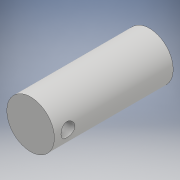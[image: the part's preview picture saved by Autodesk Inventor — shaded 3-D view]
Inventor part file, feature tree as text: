
AUTODESK INVENTOR PART (.ipt)
format: ipt  version: 2018 (Build 220112000, 112)  size: 106,496 bytes
history: native  units: mm
features: extrude x2, sketch x2
ambient origin geometry x8: Origin, YZ Plane, XZ Plane, XY Plane, X Axis, Y Axis, Z Axis, Center Point
bodies: Solide1 (feature_tree)
feature tree (4):
  extrude  "Extrusion1"  Depth=14.0mm
  extrude  "Extrusion2"  Depth=35.0mm TaperAngle=0.0deg
  sketch  "Esquisse1"
  sketch  "Esquisse2"
